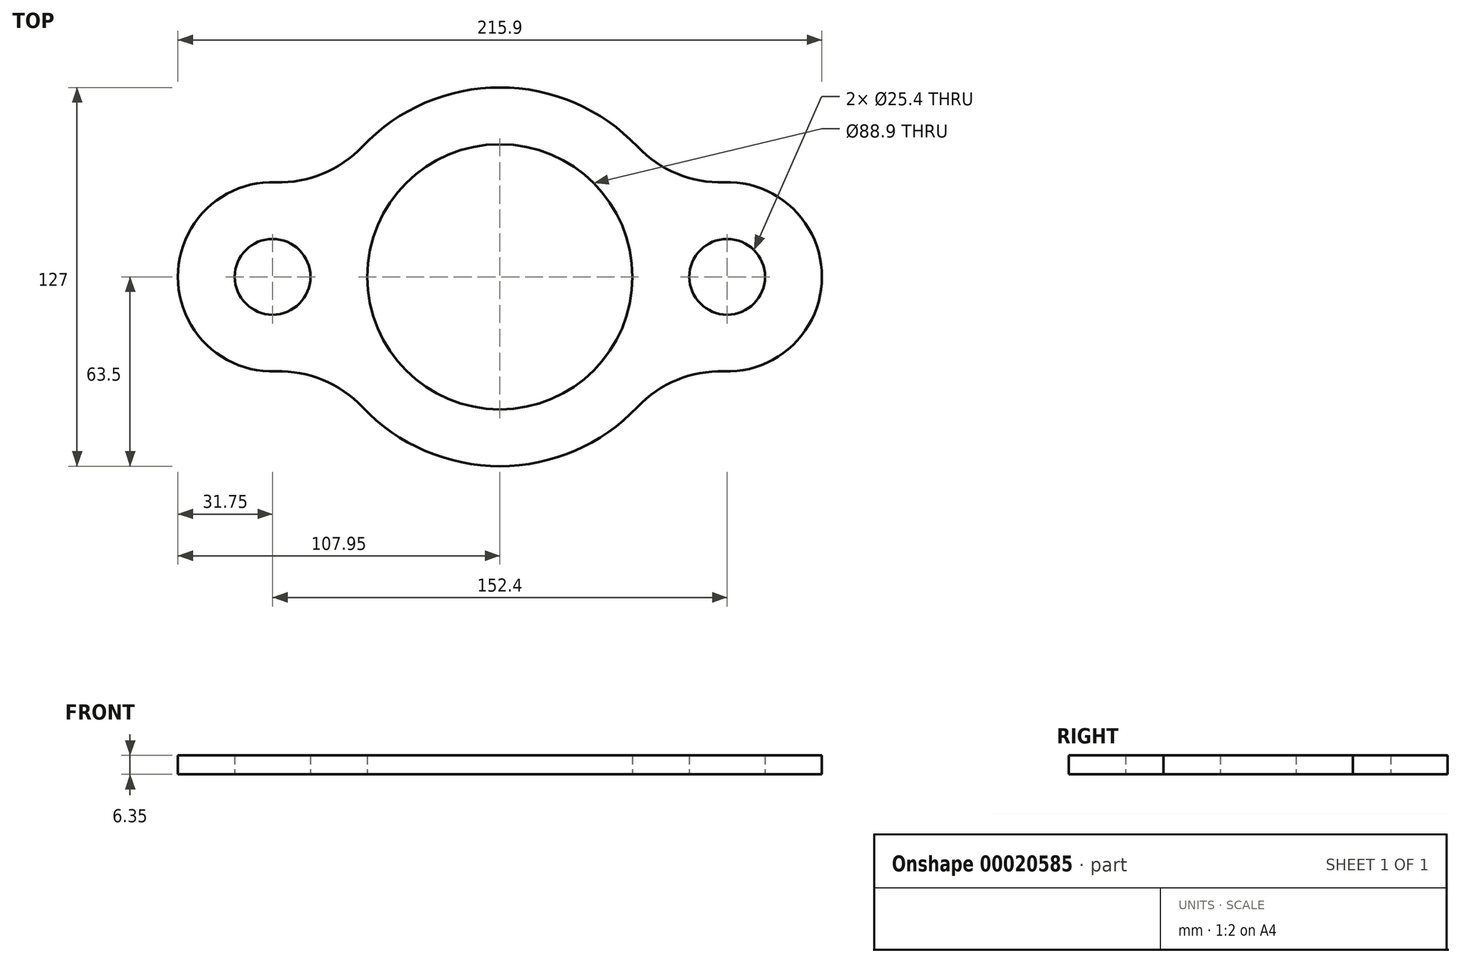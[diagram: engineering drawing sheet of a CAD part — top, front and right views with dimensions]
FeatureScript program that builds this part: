
annotation { "Feature Type Name" : "Feature", "Feature Type Description" : "" }
export const myFeature = defineFeature(function(context is Context, id is Id, definition is map)
    precondition{}
    {
        {
            var Q0;
            Q0=qCreatedBy(makeId("Top.planeOp"),FACE);
            var sketch = newSketch(context, id + "F0", { "sketchPlane" : qUnion([Q0])});
            skArc(sketch, "E0", {"start": v(-46.14, -43.63) * mm, "mid": v(0, -63.5) * mm, "end": v(46.14, -43.63) * mm});
            skCircle(sketch, "E1", {"center": v(0, 0) * mm, "radius": 44.45 * mm});
            skCircle(sketch, "E2", {"center": v(76.2, 0) * mm, "radius": 12.7 * mm});
            skCircle(sketch, "E3", {"center": v(-76.2, 0) * mm, "radius": 12.7 * mm});
            skArc(sketch, "E4", {"start": v(75.12, -31.73) * mm, "mid": v(107.95, 0) * mm, "end": v(75.12, 31.73) * mm});
            skArc(sketch, "E5", {"start": v(-75.12, 31.73) * mm, "mid": v(-107.95, 0) * mm, "end": v(-75.12, -31.73) * mm});
            skPoint(sketch, "E6.start.orphan", {"position": v(0, -44.45) * mm});
            skPoint(sketch, "E7.orphan", {"position": v(76.2, -31.75) * mm});
            skPoint(sketch, "E8.orphan", {"position": v(-76.2, -31.75) * mm});
            skArc(sketch, "E9.trimOffspring", {"start": v(46.14, 43.63) * mm, "mid": v(0, 63.5) * mm, "end": v(-46.14, 43.63) * mm});
            skPoint(sketch, "E10.visualSharp", {"position": v(-57.94, 25.98) * mm});
            skArc(sketch, "E10.filletArc", {"start": v(-75.12, 31.73) * mm, "mid": v(-59.35, 34.56) * mm, "end": v(-46.14, 43.63) * mm});
            skPoint(sketch, "E11.visualSharp", {"position": v(57.94, 25.98) * mm});
            skArc(sketch, "E11.filletArc", {"start": v(46.14, 43.63) * mm, "mid": v(59.35, 34.56) * mm, "end": v(75.12, 31.73) * mm});
            skPoint(sketch, "E12.visualSharp", {"position": v(57.94, -25.98) * mm});
            skArc(sketch, "E12.filletArc", {"start": v(75.12, -31.73) * mm, "mid": v(59.35, -34.56) * mm, "end": v(46.14, -43.63) * mm});
            skPoint(sketch, "E13.visualSharp", {"position": v(-57.94, -25.98) * mm});
            skArc(sketch, "E13.filletArc", {"start": v(-46.14, -43.63) * mm, "mid": v(-59.35, -34.56) * mm, "end": v(-75.12, -31.73) * mm});
            skSolve(sketch);
        }
        {
            var Q0;
            Q0=makeQuery(id+"F0.imprint","IMPRINT",FACE,{"disambiguationData":[TD([[makeQuery(id+"F0.imprint","IMPRINT",EDGE,{"derivedFrom":sQuery(id+"F0.wireOp",EDGE,"E0")}),1.0]])]});
            extrude(context, id + "F1", {"entities" : qUnion([Q0]), "depth" : 6.35 * mm});
        }
    });
